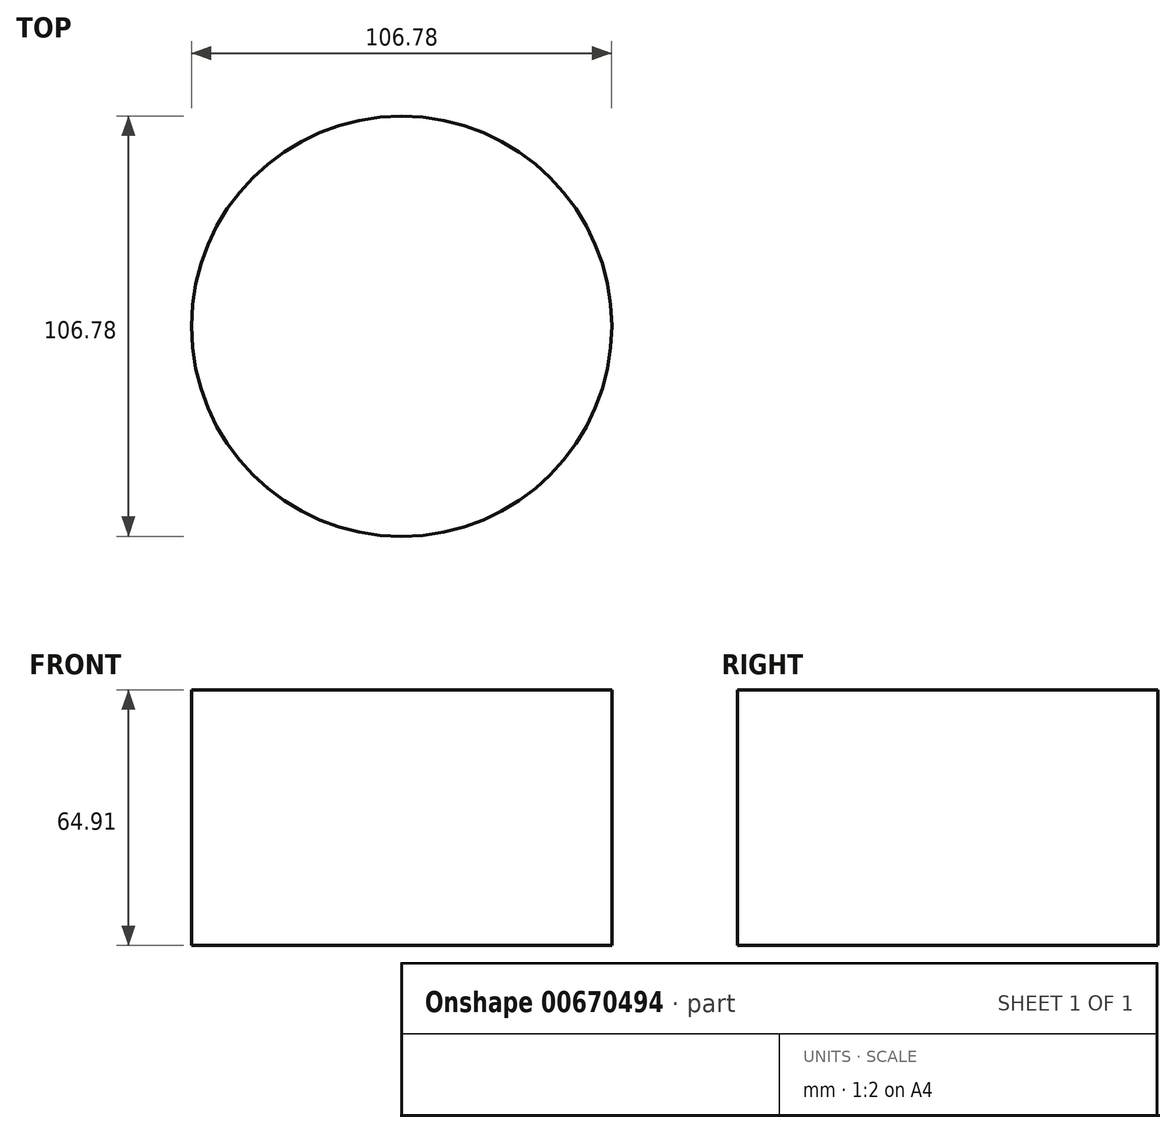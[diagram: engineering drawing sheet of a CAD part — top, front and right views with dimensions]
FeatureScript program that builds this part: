
annotation { "Feature Type Name" : "Feature", "Feature Type Description" : "" }
export const myFeature = defineFeature(function(context is Context, id is Id, definition is map)
    precondition{}
    {
        {
            var Q0;
            Q0=qCreatedBy(makeId("Top.planeOp"),FACE);
            var sketch = newSketch(context, id + "F0", { "sketchPlane" : qUnion([Q0])});
            skCircle(sketch, "E0", {"center": v(0, 0) * mm, "radius": 53.4 * mm});
            skSolve(sketch);
        }
        {
            var Q0;
            Q0=makeQuery(id+"F0.imprint","IMPRINT",FACE,{"disambiguationData":[TD([[makeQuery(id+"F0.imprint","IMPRINT",EDGE,{"derivedFrom":sQuery(id+"F0.wireOp",EDGE,"E0")}),1.0]])]});
            var Q1;
            Q1=sQuery(id+"F0.wireOp",EDGE,"E0");
            extrude(context, id + "F1", {"entities" : qUnion([Q0]), "surfaceEntities" : qUnion([Q1]), "depth" : 64.9 * mm, "offsetDistance" : 25.4 * mm});
        }
    });
